# Revit family: Deca_Lavatório de Semi-Encaixe Monte Carlo_L.82
name_source: partatom
category: Plumbing Fixtures
revit_build: Autodesk Revit Architecture 2012 (Build: 20110916_2132(x64)
units: mm (PartAtom-declared; Revit-internal decimal feet)

## types (6) — shared parameters
Aprovado por = Contino/quattroD
Assembly Code = D2010400
Atendimento ao Cliente = 0800-0117073
Criado por = Contino/quattroD
Description = Lavatório de semi-encaixe Monte Carlo
Diâmetro Ponto de Esgoto = 40 mm  [stored 0.131234 ft]
Flow Pressure = 0.00 psi
Linha = Monte Carlo
Louça/Metais = Louça
Manufacturer = Deca
Material = Deca_Vitreous China
Norma = ABNT NBR 15097-1: 2011 / ABNT NBR 15097-2: 2011 / ABNT NBR 9050:2004
Peso Liquido (Kg) = 12.9
Produto = Lavatório de semi-encaixe Monte Carlo
Raio Ponto de Esgoto = 20 mm  [stored 0.0656168 ft]
Segmento = Médio
URL = www.deca.com.br/produtos
Variações de COR = Branco (L.82.17); Creme (L.82.37); Azul (L.82.51); Verde (L.82.60); Cinza (L.82.87); Ébano (L.82..95).
zero-valued in all types: Default Elevation, WFU

## per-type parameters (varying)
| type | Código | Lavatório | Model |
| L.82.17_Branco Gelo GE17 | L.82.17 | Deca GE17 Branco Gelo Cerâmica | L.82.17 |
| L.82.95_Ébano EB95 | L.82.95 | Deca EB95 Ébano Cerâmica | L.82.95 |
| L.82.37_Creme CR37 | L.82.37 | Deca CR37 Creme Cerâmica | L.82.37 |
| L.82.51_Azul AZ51 | L.82.51 | Deca AZ51 Azul Cerâmica | L.82.51 |
| L.82.60_Verde Malva VD60 | L.82.60 | Deca VD60 Verde Malva Cerâmica | L.82.60 |
| L.82.87_Cinza Real CZ87 | L.82.87 | Deca CZ87 Cinza Real Cerâmica | L.82.87 |

note: [stored X ft] marks values corroborated as IEEE doubles in the binary element streams (Revit-internal decimal feet)

## geometry (parser evidence)
native form markers: Blend x16, Sweep x1
no freeform markers — native parametric forms only
